FCSTD DOCUMENT  (FreeCAD 0.20R25352 (Git))
Label: my gopro chest plate
License: All rights reserved
LicenseURL: http://en.wikipedia.org/wiki/All_rights_reserved
objects: Sketcher::SketchObject×1, PartDesign::Body×1
note: 2 computed .brp shape members not serialized (recipe doc carries the construction recipe); baked Part::Feature solids carry a one-line shape summary decoded from their .brp

FEATURE [Sketcher::SketchObject] Sketch
  FullyConstrained = false
  MapMode = 5
  Support = -> [XY_Plane]
  sketch-geometry (30):
    g0: ArcOfCircle CenterX=151.349 CenterY=-95.8916 CenterZ=0 NormalX=0 NormalY=0 NormalZ=1 AngleXU=0 Radius=11.3116 StartAngle=5.32703 EndAngle=8.46863
    g1: ArcOfCircle CenterX=119.675 CenterY=-118.248 CenterZ=0 NormalX=0 NormalY=0 NormalZ=1 AngleXU=0 Radius=11.3116 StartAngle=2.18544 EndAngle=5.32703
    g2: LineSegment StartX=144.826 StartY=-86.6503 StartZ=0 EndX=113.152 EndY=-109.007 EndZ=0
    g3: LineSegment StartX=126.198 StartY=-127.49 StartZ=0 EndX=157.872 EndY=-105.133 EndZ=0
    g4: ArcOfEllipse CenterX=0 CenterY=117.445 CenterZ=0 NormalX=0 NormalY=0 NormalZ=1 MajorRadius=96.4846 MinorRadius=95.8739 AngleXU=-3.14159 StartAngle=1.037 EndAngle=2.1046
    g5: LineSegment StartX=-96.4846 StartY=117.445 StartZ=0 EndX=96.4846 EndY=117.445 EndZ=0
    g6: LineSegment StartX=0 StartY=21.5711 StartZ=0 EndX=0 EndY=213.319 EndZ=0
    g7: GeomPoint X=-10.8384 Y=117.445 Z=0
    g8: GeomPoint X=10.8384 Y=117.445 Z=0
    g9: ArcOfEllipse CenterX=-215.175 CenterY=-35.4666 CenterZ=0 NormalX=0 NormalY=0 NormalZ=1 MajorRadius=162.166 MinorRadius=162.086 AngleXU=0.714662 StartAngle=5.20981 EndAngle=5.84382
    g10: LineSegment StartX=-92.6894 StartY=70.8105 StartZ=0 EndX=-337.661 EndY=-141.744 EndZ=0
    g11: LineSegment StartX=-321.4 StartY=86.959 StartZ=0 EndX=-108.951 EndY=-157.892 EndZ=0
    g12: GeomPoint X=-211.329 Y=-32.129 Z=0
    g13: GeomPoint X=-219.022 Y=-38.8042 Z=0
    g14: ArcOfEllipse CenterX=200.98 CenterY=-40.057 CenterZ=0 NormalX=0 NormalY=0 NormalZ=1 MajorRadius=155.035 MinorRadius=144.745 AngleXU=2.32404 StartAngle=0.419701 EndAngle=1.21771
    g15: LineSegment StartX=94.9348 StartY=73.0369 StartZ=0 EndX=307.025 EndY=-153.151 EndZ=0
    g16: LineSegment StartX=95.3915 StartY=-139.064 StartZ=0 EndX=306.568 EndY=58.95 EndZ=0
    g17: GeomPoint X=162.991 Y=0.456837 Z=0
    g18: GeomPoint X=238.968 Y=-80.5708 Z=0
    g19: ArcOfEllipse CenterX=-0.748188 CenterY=-238.405 CenterZ=0 NormalX=0 NormalY=0 NormalZ=1 MajorRadius=159.073 MinorRadius=158.1 AngleXU=-1.56998 StartAngle=2.71024 EndAngle=3.54808
    g20: LineSegment StartX=-0.617864 StartY=-397.477 StartZ=0 EndX=-0.878512 EndY=-79.3317 EndZ=0
    g21: LineSegment StartX=157.351 StartY=-238.275 StartZ=0 EndX=-158.848 EndY=-238.534 EndZ=0
    g22: GeomPoint X=-0.733793 Y=-255.975 Z=0
    g23: GeomPoint X=-0.762583 Y=-220.834 Z=0
    g24: Circle CenterX=-49.0922 CenterY=34.9091 CenterZ=0 NormalX=0 NormalY=0 NormalZ=1 AngleXU=0 Radius=1
    g25: Circle CenterX=-63.7485 CenterY=42.1801 CenterZ=0 NormalX=0 NormalY=0 NormalZ=1 AngleXU=0 Radius=1
    g26: Circle CenterX=-59.1388 CenterY=8.64162 CenterZ=0 NormalX=0 NormalY=0 NormalZ=1 AngleXU=0 Radius=1
    g27: BSplineCurve PolesCount=3 KnotsCount=2 Degree=2 IsPeriodic=0
    g28: GeomPoint X=-49.0922 Y=34.9091 Z=0
    g29: GeomPoint X=-59.1388 Y=8.64162 Z=0
  constraints (24):
    c: Tangent(g0,g2) = -1.5708
    c: Tangent(g2,g1) = -1.5708
    c: Tangent(g1,g3) = -1.5708
    c: Tangent(g3,g0) = -1.5708
    c: Equal(g0,g1)
    c: InternalAlignment(g5-g8 -> g4) x4
    c: PointOnObject(g4,g-2)
    c: Horizontal(g4,g4)
    c: Horizontal(g5,g5)
    c: InternalAlignment(g10-g13 -> g9) x4
    c: InternalAlignment(g15-g18 -> g14) x4
    c: InternalAlignment(g20-g23 -> g19) x4
    c: Coincident(g19,g9)
    c: Coincident(g19,g14)
    c: Coincident(g27,g4)
    c: Weight(g24) = 1
    c: Equal(g24,g25)
    c: Equal(g24,g26)
    c: Coincident(g27,g9)
    c: InternalAlignment(g24,g27)
    c: InternalAlignment(g25,g27)
    c: InternalAlignment(g26,g27)
    c: InternalAlignment(g28,g27)
    c: InternalAlignment(g29,g27)
FEATURE [PartDesign::Body] Body
  Group = -> [Sketch]
  Origin = -> Origin
